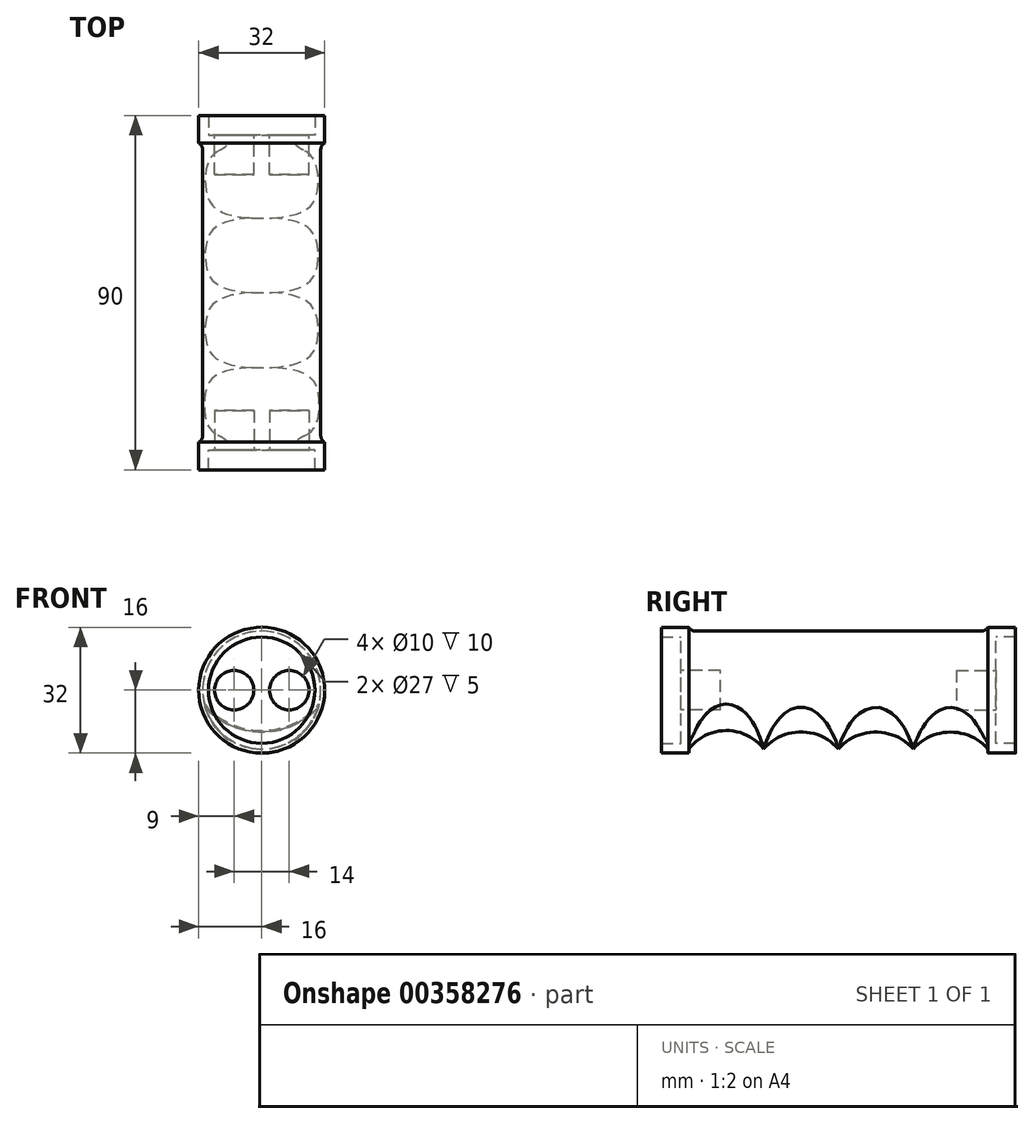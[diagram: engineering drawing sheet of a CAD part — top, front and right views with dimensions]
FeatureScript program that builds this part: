
annotation { "Feature Type Name" : "Feature", "Feature Type Description" : "" }
export const myFeature = defineFeature(function(context is Context, id is Id, definition is map)
    precondition{}
    {
        {
            var Q0;
            Q0=qCreatedBy(makeId("Front.planeOp"),FACE);
            var sketch = newSketch(context, id + "F0", { "sketchPlane" : qUnion([Q0])});
            skCircle(sketch, "E0", {"center": v(0, 0) * mm, "radius": 15 * mm});
            skSolve(sketch);
        }
        {
            var Q0;
            Q0 = qSketchRegion(id + "F0", true);
            extrude(context, id + "F1", {"entities" : qUnion([Q0]), "endBound" : BoundingType.SYMMETRIC, "depth" : 80 * mm});
        }
        {
            var Q0;
            Q0=qCreatedBy(makeId("Front.planeOp"),FACE);
            var sketch = newSketch(context, id + "F2", { "sketchPlane" : qUnion([Q0])});
            skArc(sketch, "E1", {"start": v(0, -12.5) * mm, "mid": v(5.8, 29.6) * mm, "end": v(-11.16, -9.37) * mm});
            skArc(sketch, "E2", {"start": v(-11.16, -9.37) * mm, "mid": v(-5.8, -11.7) * mm, "end": v(0, -12.5) * mm});
            skSolve(sketch);
        }
        {
            var Q0;
            Q0=qCreatedBy(makeId("Right.planeOp"),FACE);
            var sketch = newSketch(context, id + "F3", { "sketchPlane" : qUnion([Q0])});
            skArc(sketch, "E3", {"start": v(-19, -14.92) * mm, "mid": v(-28.5, -10.25) * mm, "end": v(-38, -14.92) * mm});
            skArc(sketch, "E4", {"start": v(0, -14.92) * mm, "mid": v(-9.5, -10.6) * mm, "end": v(-19, -14.92) * mm});
            skArc(sketch, "E5", {"start": v(19, -14.92) * mm, "mid": v(9.5, -10.63) * mm, "end": v(0, -14.92) * mm});
            skArc(sketch, "E6", {"start": v(38, -14.92) * mm, "mid": v(28.5, -10.64) * mm, "end": v(19, -14.92) * mm});
            skLineSegment(sketch, "E7.top", {"start": v(-38, -16.12) * mm, "end": v(38, -16.12) * mm});
            skLineSegment(sketch, "E7.left", {"start": v(-38, -14.92) * mm, "end": v(-38, -16.12) * mm});
            skLineSegment(sketch, "E7.right", {"start": v(38, -14.92) * mm, "end": v(38, -16.12) * mm});
            skSolve(sketch);
        }
        {
            var Q0;
            Q0=makeQuery(id+"F1.opExtrude","CAP_FACE",FACE,{"disambiguationData":[OSD([sQuery(id+"F0.wireOp",EDGE,"E0")])],"isStart":false});
            var sketch = newSketch(context, id + "F4", { "sketchPlane" : qUnion([Q0])});
            skCircle(sketch, "E8", {"center": v(0, 0) * mm, "radius": 16 * mm});
            skCircle(sketch, "E9", {"center": v(0, 0) * mm, "radius": 13.5 * mm});
            skLineSegment(sketch, "E10", {"start": v(0, 0) * mm, "end": v(7, 0) * mm});
            skLineSegment(sketch, "E11", {"start": v(0, 0) * mm, "end": v(-7, 0) * mm});
            skCircle(sketch, "E12", {"center": v(-7, 0) * mm, "radius": 5 * mm});
            skCircle(sketch, "E13", {"center": v(7, 0) * mm, "radius": 5 * mm});
            skSolve(sketch);
        }
        {
            var Q0;
            Q0=makeQuery(id+"F4.imprint","IMPRINT",FACE,{"disambiguationData":[TD([[makeQuery(id+"F4.imprint","IMPRINT",EDGE,{"derivedFrom":sQuery(id+"F4.wireOp",EDGE,"E9")}),-1.0]])]});
            var Q1;
            Q1=makeQuery(id+"F4.imprint","IMPRINT",FACE,{"disambiguationData":[TD([[makeQuery(id+"F4.imprint","IMPRINT",EDGE,{"derivedFrom":sQuery(id+"F4.wireOp",EDGE,"E8")}),1.0]])]});
            extrude(context, id + "F5", {"entities" : qUnion([Q0, Q1]), "operationType" : NewBodyOperationType.ADD, "depth" : 5 * mm, "hasSecondDirection" : true, "secondDirectionOppositeDirection" : true, "secondDirectionDepth" : 2 * mm});
        }
        {
            var Q0;
            Q0=makeQuery(id+"F4.imprint","IMPRINT",FACE,{"disambiguationData":[TD([[makeQuery(id+"F4.imprint","IMPRINT",EDGE,{"derivedFrom":sQuery(id+"F4.wireOp",EDGE,"E13")}),1.0]])]});
            var Q1;
            Q1=makeQuery(id+"F4.imprint","IMPRINT",FACE,{"disambiguationData":[TD([[makeQuery(id+"F4.imprint","IMPRINT",EDGE,{"derivedFrom":sQuery(id+"F4.wireOp",EDGE,"E12")}),1.0]])]});
            extrude(context, id + "F6", {"entities" : qUnion([Q0, Q1]), "operationType" : NewBodyOperationType.REMOVE, "oppositeDirection" : true, "depth" : 10 * mm});
        }
        {
            var Q0;
            Q0=makeQuery(id+"F1.opExtrude","CAP_FACE",FACE,{"disambiguationData":[OSD([sQuery(id+"F0.wireOp",EDGE,"E0")])],"isStart":true});
            var sketch = newSketch(context, id + "F7", { "sketchPlane" : qUnion([Q0])});
            skCircle(sketch, "E14", {"center": v(0, 0) * mm, "radius": 16 * mm});
            skCircle(sketch, "E15", {"center": v(0, 0) * mm, "radius": 13.5 * mm});
            skLineSegment(sketch, "E16", {"start": v(0, 0) * mm, "end": v(-7, 0) * mm});
            skLineSegment(sketch, "E17", {"start": v(0, 0) * mm, "end": v(7, 0) * mm});
            skCircle(sketch, "E18", {"center": v(-7, 0) * mm, "radius": 5 * mm});
            skCircle(sketch, "E19", {"center": v(7, 0) * mm, "radius": 5 * mm});
            skSolve(sketch);
        }
        {
            var Q0;
            Q0=makeQuery(id+"F7.imprint","IMPRINT",FACE,{"disambiguationData":[TD([[makeQuery(id+"F7.imprint","IMPRINT",EDGE,{"derivedFrom":sQuery(id+"F7.wireOp",EDGE,"E14")}),1.0]])]});
            var Q1;
            Q1=makeQuery(id+"F7.imprint","IMPRINT",FACE,{"disambiguationData":[TD([[makeQuery(id+"F7.imprint","IMPRINT",EDGE,{"derivedFrom":sQuery(id+"F7.wireOp",EDGE,"E15")}),-1.0]])]});
            extrude(context, id + "F8", {"entities" : qUnion([Q0, Q1]), "operationType" : NewBodyOperationType.ADD, "depth" : 5 * mm, "hasSecondDirection" : true, "secondDirectionOppositeDirection" : true, "secondDirectionDepth" : 2 * mm});
        }
        {
            var Q0;
            Q0=makeQuery(id+"F7.imprint","IMPRINT",FACE,{"disambiguationData":[TD([[makeQuery(id+"F7.imprint","IMPRINT",EDGE,{"derivedFrom":sQuery(id+"F7.wireOp",EDGE,"E19")}),1.0]])]});
            var Q1;
            Q1=makeQuery(id+"F7.imprint","IMPRINT",FACE,{"disambiguationData":[TD([[makeQuery(id+"F7.imprint","IMPRINT",EDGE,{"derivedFrom":sQuery(id+"F7.wireOp",EDGE,"E18")}),1.0]])]});
            extrude(context, id + "F9", {"entities" : qUnion([Q0, Q1]), "operationType" : NewBodyOperationType.REMOVE, "oppositeDirection" : true, "depth" : 10 * mm});
        }
        {
            var Q0;
            Q0 = qSketchRegion(id + "F3", true);
            var Q1;
            Q1=sQuery(id+"F2.wireOp",EDGE,"E2");
            var Q2;
            Q2=sQuery(id+"F2.wireOp",EDGE,"E1");
            sweep(context, id + "F10", {"operationType" : NewBodyOperationType.REMOVE, "profiles" : qUnion([Q0]), "path" : qUnion([Q1, Q2])});
        }
        {
            var Q0;
            Q0=makeQuery(id+"F5.boolean.opBoolean","INTERSECT",EDGE,{"derivedFrom":[makeQuery(id+"F1.opExtrude","SWEPT_FACE",FACE,{"disambiguationData":[OSD([sQuery(id+"F0.wireOp",EDGE,"E0")])]}),makeQuery(id+"F5.opExtrude","CAP_FACE",FACE,{"disambiguationData":[OSD([sQuery(id+"F4.wireOp",EDGE,"E8"),sQuery(id+"F4.wireOp",EDGE,"E9")])],"isStart":true})]});
            var Q1;
            Q1=makeQuery(id+"F10.boolean.opBoolean","COPY",EDGE,{"derivedFrom":makeQuery(id+"F10.opSweep","SWEPT_EDGE",EDGE,{"disambiguationData":[OSD([sQuery(id+"F2.wireOp",EDGE,"E1"),sQuery(id+"F3.wireOp",EDGE,"E3"),sQuery(id+"F3.wireOp",EDGE,"E7.left")])]})});
            fillet(context, id + "F11", {"entities" : qUnion([Q0, Q1]), "radius" : 2 * mm, "tangentPropagation" : true, "allowEdgeOverflow" : false});
        }
        {
            var Q0;
            Q0=makeQuery(id+"F8.boolean.opBoolean","INTERSECT",EDGE,{"derivedFrom":[makeQuery(id+"F1.opExtrude","SWEPT_FACE",FACE,{"disambiguationData":[OSD([sQuery(id+"F0.wireOp",EDGE,"E0")])]}),makeQuery(id+"F8.opExtrude","CAP_FACE",FACE,{"disambiguationData":[OSD([sQuery(id+"F7.wireOp",EDGE,"E14"),sQuery(id+"F7.wireOp",EDGE,"E15")])],"isStart":true})]});
            var Q1;
            Q1=makeQuery(id+"F10.boolean.opBoolean","COPY",EDGE,{"derivedFrom":makeQuery(id+"F10.opSweep","SWEPT_EDGE",EDGE,{"disambiguationData":[OSD([sQuery(id+"F2.wireOp",EDGE,"E1"),sQuery(id+"F3.wireOp",EDGE,"E6"),sQuery(id+"F3.wireOp",EDGE,"E7.right")])]})});
            fillet(context, id + "F12", {"entities" : qUnion([Q0, Q1]), "radius" : 2 * mm, "tangentPropagation" : true, "allowEdgeOverflow" : false});
        }
    });
